AUTODESK INVENTOR PART (.ipt)
format: ipt  version: 2022 (Build 260153070, 153G)  size: 435,712 bytes
history: native  units: mm
features: other x31, plane x16, sketch x5
ambient origin geometry x8: Origin, YZ Plane, XZ Plane, XY Plane, X Axis, Y Axis, Z Axis, Center Point
feature tree (52):
  other  "Blocks"
  other  "Side"
  other  "Front_USB_Lip"
  sketch  "Sketch12"  dims[d51=50.0mm]
  plane  "Work Plane - PCB_Top"
  plane  "Work Plane1"
  other  "Bottom"
  other  "PCB"
  plane  "Work Plane16"
  other  "Fan_Side"
  plane  "Work Plane17"
  other  "Fan_Front"
  plane  "Work Plane2"
  plane  "Work Plane - Screen_Top"
  other  "Top_Housing"
  plane  "Work Plane18"
  other  "Side_Camera"
  other  "Screen_Hole"
  other  "Cover_Mount"
  sketch  "Sketch20"  dims[d53=15.0deg]
  plane  "Work Plane - Mount_Post"
  other  "Mount_Post"
  sketch  "Sketch10"  dims[d16=200.0mm]
  plane  "Work Plane7"
  plane  "Work Plane9"
  other  "Power_HDMI_Connectors"
  plane  "Work Plane11"
  other  "PCB_USB_Con"
  plane  "Work Plane - TH_Bottom_Edge"
  other  "Top_Housing_Bottom_Edge"
  other  "Fan_Top"
  plane  "Work Plane14"
  other  "USB_Position"
  plane  "Work Plane19"
  other  "USB_Side"
  plane  "Work Plane15"
  sketch  "Sketch25"  dims[d61=22.0mm]
  plane  "Work Plane20"
  sketch  "Sketch29"  dims[d67=193.5mm d68=111.3mm d69=1.9mm d70=12.0mm d78=5.0mm d84=2.0mm d85=2.0mm d86=22.0mm d87=10.0mm d88=2.0mm d89=56.0mm d90=1.2mm d92=3.0mm d93=85.0mm d96=49.0mm d97=2.8mm d98=58.0mm d99=3.5mm d100=1.2mm d101=6.93mm d102=2.98mm d109=50.0mm d110=6.0mm d111=7.0mm d121=25.0mm d122=18.0mm d124=20.0mm d125=1.0mm d126=2.0mm d130=2.0mm d131=2.0mm d133=2.0mm d135=13.2mm d136=13.2mm d139=15.0mm d141=13.6mm d142=16.0mm d145=70.0mm d148=6.0mm d150=9.0mm d151=4.5mm d152=7.0mm d153=10.0mm d154=9.0mm d155=11.0mm d156=11.0mm d158=88.00914mm d159=0.349066mm d160=3.5mm d161=1.5mm d162=3.5mm d163=16.580628mm d165=3.5mm d166=2.0mm d167=28.0mm d168=55.0mm d169=0.349066mm d170=0.349066mm d171=0.2mm d172=2.0mm d174=2.0mm d177=3.5mm d178=18.5mm d179=3.5mm d180=19.198622mm d182=33.0mm d185=5.0mm d186=5.0mm d187=8.0mm d188=24.0mm d189=25.0mm d190=60.0mm d194=9.5mm d198=19.0mm d200=15.0mm d201=21.0mm d202=2.0mm d203=12.5mm d204=2.1mm d206=1.0mm d209=30.0mm d210=2.5mm d211=6.5mm d215=126.2mm d217=23.53mm d218=65.65mm d219=18.0mm d221=34.87mm d222=10.1mm d224=6.3mm d225=96.9mm d227=30.0mm d235=50.0mm d236=16.0mm d239=100.0mm d241=22.0mm d242=5.0mm d243=25.6mm d244=1.0mm d245=4.2mm d246=9.0mm d247=21.7mm d248=15.0mm d249=15.0mm d250=25.0mm d251=3.3mm d252=11.5mm d253=29.8mm d254=25.0mm d255=7.0mm d256=25.0mm d257=12.0mm d258=1.0mm d259=25.0mm d260=7.0mm d261=10.0mm d263=3.0mm d264=8.0mm d265=4.0mm d266=3.0mm d267=15.882496mm d268=3.0mm d269=22.0mm d270=11.5mm d271=8.5mm d272=10.2mm d273=5.7mm d274=7.0mm d275=0.4mm d276=10.0mm d278=0.5mm d279=13.2mm d280=17.6mm d281=0.2mm d282=0.2mm d284=7.5mm d285=6.0mm d286=19.198622mm d287=19.198622mm d288=1.5mm d289=2.0mm d291=20.071286mm d292=2.0mm d293=0.5mm d294=20.071286mm d295=14.660766mm d296=0.7mm d297=3.0mm d298=2.5mm d300=1.5mm d301=15.882496mm d302=15.882496mm d304=6.5mm d306=15.53343mm d307=0.3mm d309=4.0mm d312=22.0mm d313=0.2mm d314=12.0mm d315=13.0mm d316=60.0mm d318=3.490659mm d320=15.53343mm d321=1.0mm d325=25.0mm d327=3.0mm d332=3.5mm d333=15.0mm d334=15.358897mm d335=102.0mm d336=5.0mm d337=0.2mm d338=2.0mm d340=22.6mm d341=2.7mm d342=29.2mm d343=36.0mm d344=42.9mm d345=0.5mm d346=1.0mm d347=3.0mm d348=72.0mm d349=4.201288mm d351=101.0mm d352=3.0mm d353=101.0mm d354=3.0mm d355=0.2mm]
  other  "USB_Hole_Top_Cover"
  other  "Block1"
  other  "Block2"
  other  "RPI"
  other  "Ports "
  other  "USB_Ports"
  other  "Camera_Top"
  other  "Block2:1"
  other  "Block2:2"
  other  "RPI:1"
  other  "USB_Ports:1"
  other  "Ports :2"
  other  "Camera_Top:1"
